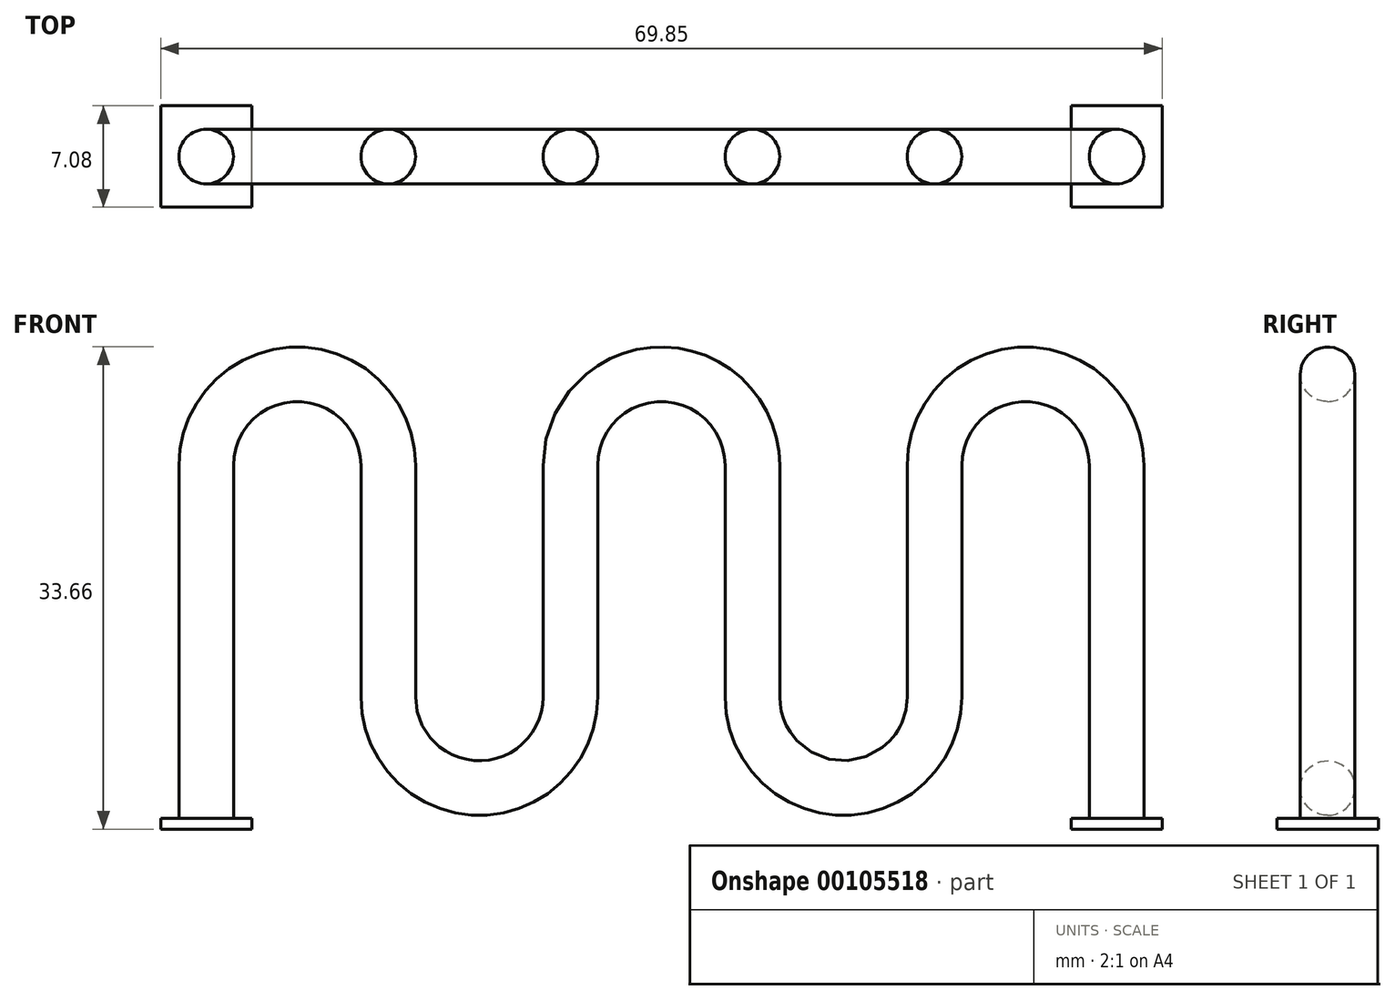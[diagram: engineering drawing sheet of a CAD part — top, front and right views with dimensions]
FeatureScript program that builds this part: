
annotation { "Feature Type Name" : "Feature", "Feature Type Description" : "" }
export const myFeature = defineFeature(function(context is Context, id is Id, definition is map)
    precondition{}
    {
        {
            var Q0;
            Q0=qCreatedBy(makeId("Front.planeOp"),FACE);
            var sketch = newSketch(context, id + "F0", { "sketchPlane" : qUnion([Q0])});
            skLineSegment(sketch, "E0", {"start": v(-70.59, 0) * mm, "end": v(-70.59, 25.4) * mm});
            skLineSegment(sketch, "E1", {"start": v(-57.89, 25.4) * mm, "end": v(-57.89, 9.22) * mm});
            skLineSegment(sketch, "E2", {"start": v(-45.19, 9.22) * mm, "end": v(-45.19, 25.4) * mm});
            skLineSegment(sketch, "E3", {"start": v(-32.49, 25.4) * mm, "end": v(-32.49, 9.22) * mm});
            skLineSegment(sketch, "E4", {"start": v(-19.79, 9.22) * mm, "end": v(-19.79, 25.4) * mm});
            skLineSegment(sketch, "E5", {"start": v(-7.09, 25.4) * mm, "end": v(-7.09, 0) * mm});
            skArc(sketch, "E6", {"start": v(-57.89, 25.4) * mm, "mid": v(-64.24, 31.75) * mm, "end": v(-70.59, 25.4) * mm});
            skArc(sketch, "E7", {"start": v(-57.89, 9.22) * mm, "mid": v(-51.54, 2.87) * mm, "end": v(-45.19, 9.22) * mm});
            skArc(sketch, "E8", {"start": v(-32.49, 25.4) * mm, "mid": v(-38.84, 31.75) * mm, "end": v(-45.19, 25.4) * mm});
            skArc(sketch, "E9", {"start": v(-32.49, 9.22) * mm, "mid": v(-26.14, 2.87) * mm, "end": v(-19.79, 9.22) * mm});
            skArc(sketch, "E10", {"start": v(-7.09, 25.4) * mm, "mid": v(-13.44, 31.75) * mm, "end": v(-19.79, 25.4) * mm});
            skSolve(sketch);
        }
        {
            var Q0;
            Q0=qCreatedBy(makeId("Top.planeOp"),FACE);
            var sketch = newSketch(context, id + "F1", { "sketchPlane" : qUnion([Q0])});
            skCircle(sketch, "E11", {"center": v(-70.59, 0) * mm, "radius": 1.9 * mm});
            skCircle(sketch, "E12", {"center": v(-7.09, 0) * mm, "radius": 1.9 * mm});
            skLineSegment(sketch, "E13.bottom", {"start": v(-67.41, -3.54) * mm, "end": v(-73.76, -3.54) * mm});
            skLineSegment(sketch, "E13.top", {"start": v(-67.41, 3.54) * mm, "end": v(-73.76, 3.54) * mm});
            skLineSegment(sketch, "E13.left", {"start": v(-67.41, -3.54) * mm, "end": v(-67.41, 3.54) * mm});
            skLineSegment(sketch, "E13.right", {"start": v(-73.76, -3.54) * mm, "end": v(-73.76, 3.54) * mm});
            skLineSegment(sketch, "E14.bottom", {"start": v(-3.91, -3.54) * mm, "end": v(-10.26, -3.54) * mm});
            skLineSegment(sketch, "E14.top", {"start": v(-3.91, 3.54) * mm, "end": v(-10.26, 3.54) * mm});
            skLineSegment(sketch, "E14.left", {"start": v(-3.91, -3.54) * mm, "end": v(-3.91, 3.54) * mm});
            skLineSegment(sketch, "E14.right", {"start": v(-10.26, -3.54) * mm, "end": v(-10.26, 3.54) * mm});
            skSolve(sketch);
        }
        {
            var Q0;
            Q0=makeQuery(id+"F1.imprint","IMPRINT",FACE,{"disambiguationData":[TD([[makeQuery(id+"F1.imprint","IMPRINT",EDGE,{"derivedFrom":sQuery(id+"F1.wireOp",EDGE,"E11")}),1.0]])]});
            var Q1;
            Q1=sQuery(id+"F0.wireOp",EDGE,"E0");
            var Q2;
            Q2=sQuery(id+"F0.wireOp",EDGE,"E6");
            var Q3;
            Q3=sQuery(id+"F0.wireOp",EDGE,"E1");
            var Q4;
            Q4=sQuery(id+"F0.wireOp",EDGE,"E7");
            var Q5;
            Q5=sQuery(id+"F0.wireOp",EDGE,"E2");
            var Q6;
            Q6=sQuery(id+"F0.wireOp",EDGE,"E8");
            var Q7;
            Q7=sQuery(id+"F0.wireOp",EDGE,"E3");
            var Q8;
            Q8=sQuery(id+"F0.wireOp",EDGE,"E9");
            var Q9;
            Q9=sQuery(id+"F0.wireOp",EDGE,"E4");
            var Q10;
            Q10=sQuery(id+"F0.wireOp",EDGE,"E10");
            var Q11;
            Q11=sQuery(id+"F0.wireOp",EDGE,"E5");
            sweep(context, id + "F2", {"profiles" : qUnion([Q0]), "path" : qUnion([Q1, Q2, Q3, Q4, Q5, Q6, Q7, Q8, Q9, Q10, Q11])});
        }
        {
            var Q0;
            Q0=makeQuery(id+"F1.imprint","IMPRINT",FACE,{"disambiguationData":[TD([[makeQuery(id+"F1.imprint","IMPRINT",EDGE,{"derivedFrom":sQuery(id+"F1.wireOp",EDGE,"E11")}),-1.0]])]});
            var Q1;
            Q1=makeQuery(id+"F1.imprint","IMPRINT",FACE,{"disambiguationData":[TD([[makeQuery(id+"F1.imprint","IMPRINT",EDGE,{"derivedFrom":sQuery(id+"F1.wireOp",EDGE,"E12")}),-1.0]])]});
            extrude(context, id + "F3", {"entities" : qUnion([Q0, Q1]), "operationType" : NewBodyOperationType.ADD, "depth" : 0.76 * mm});
        }
    });
